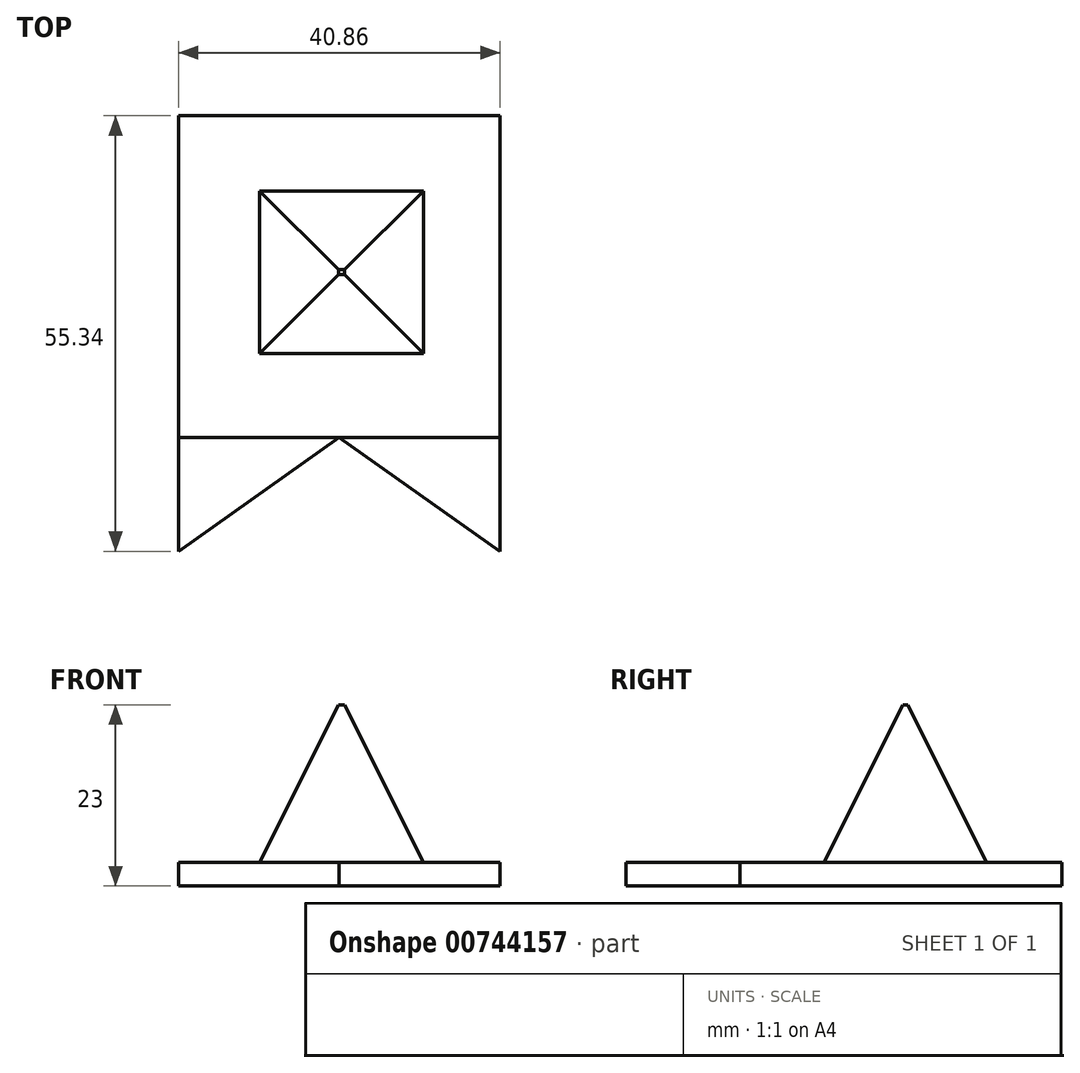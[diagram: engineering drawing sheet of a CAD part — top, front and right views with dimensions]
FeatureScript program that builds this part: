
annotation { "Feature Type Name" : "Feature", "Feature Type Description" : "" }
export const myFeature = defineFeature(function(context is Context, id is Id, definition is map)
    precondition{}
    {
        {
            var Q0;
            Q0=qCreatedBy(makeId("Top.planeOp"),FACE);
            var sketch = newSketch(context, id + "F0", { "sketchPlane" : qUnion([Q0])});
            skLineSegment(sketch, "E0.bottom", {"start": v(-38.77, 31.2) * mm, "end": v(-17.98, 31.2) * mm});
            skLineSegment(sketch, "E0.top", {"start": v(-38.77, 10.55) * mm, "end": v(-17.98, 10.55) * mm});
            skLineSegment(sketch, "E0.left", {"start": v(-38.77, 31.2) * mm, "end": v(-38.77, 10.55) * mm});
            skLineSegment(sketch, "E0.right", {"start": v(-17.98, 31.2) * mm, "end": v(-17.98, 10.55) * mm});
            skSolve(sketch);
        }
        {
            var Q0;
            Q0 = qSketchRegion(id + "F0", true);
            extrude(context, id + "F1", {"entities" : qUnion([Q0]), "depth" : 20 * mm, "offsetDistance" : 25 * mm});
        }
        {
            var Q0;
            Q0=makeQuery(id+"F1.opExtrude","CAP_EDGE",EDGE,{"disambiguationData":[OSD([sQuery(id+"F0.wireOp",EDGE,"E0.right")])],"isStart":false});
            var Q1;
            Q1=makeQuery(id+"F1.opExtrude","CAP_EDGE",EDGE,{"disambiguationData":[OSD([sQuery(id+"F0.wireOp",EDGE,"E0.left")])],"isStart":false});
            var Q2;
            Q2=makeQuery(id+"F1.opExtrude","CAP_EDGE",EDGE,{"disambiguationData":[OSD([sQuery(id+"F0.wireOp",EDGE,"E0.top")])],"isStart":false});
            var Q3;
            Q3=makeQuery(id+"F1.opExtrude","CAP_EDGE",EDGE,{"disambiguationData":[OSD([sQuery(id+"F0.wireOp",EDGE,"E0.bottom")])],"isStart":false});
            chamfer(context, id + "F2", {"entities" : qUnion([Q0, Q1, Q2, Q3]), "chamferType" : ChamferType.TWO_OFFSETS, "width1" : 20 * mm, "oppositeDirection" : false, "width2" : 10 * mm, "tangentPropagation" : true});
        }
        {
            var Q0;
            Q0=makeQuery(id+"F1.opExtrude","CAP_FACE",FACE,{"disambiguationData":[OSD([sQuery(id+"F0.wireOp",EDGE,"E0.bottom"),sQuery(id+"F0.wireOp",EDGE,"E0.top"),sQuery(id+"F0.wireOp",EDGE,"E0.left"),sQuery(id+"F0.wireOp",EDGE,"E0.right")])],"isStart":true});
            var sketch = newSketch(context, id + "F3", { "sketchPlane" : qUnion([Q0])});
            skLineSegment(sketch, "E1.bottom", {"start": v(-8.23, -40.76) * mm, "end": v(-49.1, -40.76) * mm});
            skLineSegment(sketch, "E1.top", {"start": v(-8.23, 0.1) * mm, "end": v(-49.1, 0.1) * mm});
            skLineSegment(sketch, "E1.left", {"start": v(-8.23, -40.76) * mm, "end": v(-8.23, 0.1) * mm});
            skLineSegment(sketch, "E1.right", {"start": v(-49.1, -40.76) * mm, "end": v(-49.1, 0.1) * mm});
            skPoint(sketch, "E1.middle", {"position": v(-28.66, -20.33) * mm});
            skSolve(sketch);
        }
        {
            var Q0;
            Q0 = qSketchRegion(id + "F3", true);
            extrude(context, id + "F4", {"entities" : qUnion([Q0]), "operationType" : NewBodyOperationType.ADD, "depth" : 3 * mm, "offsetDistance" : 25 * mm});
        }
        {
            var Q0;
            Q0=makeQuery(id+"F4.opExtrude","CAP_FACE",FACE,{"disambiguationData":[OSD([sQuery(id+"F3.wireOp",EDGE,"E1.bottom"),sQuery(id+"F3.wireOp",EDGE,"E1.top"),sQuery(id+"F3.wireOp",EDGE,"E1.left"),sQuery(id+"F3.wireOp",EDGE,"E1.right")])],"isStart":false});
            var sketch = newSketch(context, id + "F5", { "sketchPlane" : qUnion([Q0])});
            skLineSegment(sketch, "E2", {"start": v(-49.1, 0.1) * mm, "end": v(-49.1, 14.58) * mm});
            skLineSegment(sketch, "E3", {"start": v(-49.1, 14.58) * mm, "end": v(-28.66, 0.1) * mm});
            skLineSegment(sketch, "E4", {"start": v(-28.66, 0.1) * mm, "end": v(-49.1, 0.1) * mm});
            skLineSegment(sketch, "E5", {"start": v(-28.66, 0.1) * mm, "end": v(-8.23, 14.58) * mm});
            skLineSegment(sketch, "E6", {"start": v(-8.23, 14.58) * mm, "end": v(-8.23, 0.1) * mm});
            skLineSegment(sketch, "E7", {"start": v(-8.23, 0.1) * mm, "end": v(-49.1, 0.1) * mm});
            skSolve(sketch);
        }
        {
            var Q0;
            {var subQ0=sQuery(id+"F5.wireOp",EDGE,"E2");Q0=makeQuery(id+"F5.imprint","IMPRINT",FACE,{"disambiguationData":[TD([[makeQuery(id+"F5.imprint","IMPRINT",EDGE,{"derivedFrom":subQ0}),-1.0]])]});}
            var Q1;
            {var subQ0=sQuery(id+"F5.wireOp",EDGE,"E5");Q1=makeQuery(id+"F5.imprint","IMPRINT",FACE,{"disambiguationData":[TD([[makeQuery(id+"F5.imprint","IMPRINT",EDGE,{"derivedFrom":subQ0}),-1.0]])]});}
            extrude(context, id + "F6", {"entities" : qUnion([Q0, Q1]), "oppositeDirection" : true, "depth" : 3 * mm, "offsetDistance" : 25 * mm});
        }
    });
